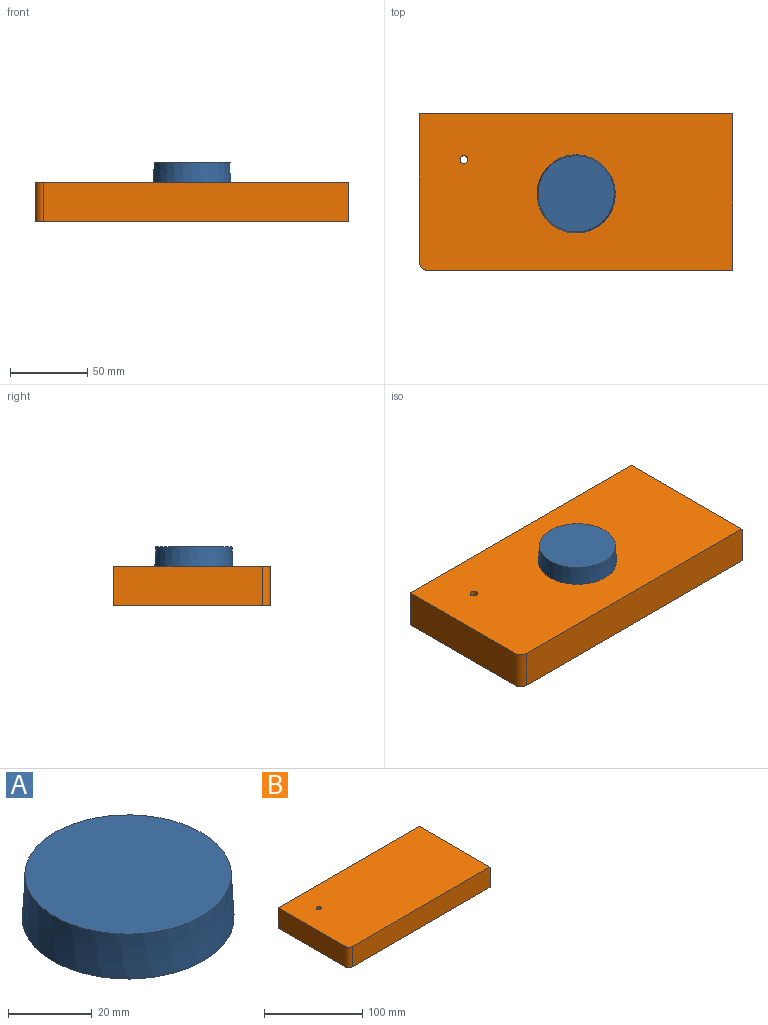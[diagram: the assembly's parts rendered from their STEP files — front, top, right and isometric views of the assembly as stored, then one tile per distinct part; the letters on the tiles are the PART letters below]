
ASSEMBLY  parts=2 mates=1
PART A: 3 faces, bbox 50.8x50.8x12.7 mm
  f0: plane 50.8x50.8mm, normal (0,0,-1), area 2026.8mm2, adj f1
  f1: cone r=25.4mm half-angle=3deg, axis (0,0,-1), area 2003mm2, adj f0,f2
  f2: plane 49.47x49.47mm, normal (0,0,1), area 1922mm2, adj f1
PART B: 8 faces, bbox 203.2x101.6x25.4 mm
  f0: plane 96.52x25.4mm, normal (-1,0,0), area 2451.6mm2, adj f3,f4,f5,f7
  f1: plane 198.12x25.4mm, normal (0,-1,0), area 5032.2mm2, adj f2,f4,f5,f7
  f2: plane 101.6x25.4mm, normal (1,0,0), area 2580.6mm2, adj f1,f3,f4,f5
  f3: plane 203.2x25.4mm, normal (0,1,0), area 5161.3mm2, adj f0,f2,f4,f5
  f4: plane 203.2x101.6mm, normal (0,0,1), area 20619.1mm2, adj f0,f1,f2,f3,f6,f7
  f5: plane 203.2x101.6mm, normal (0,0,-1), area 20619.1mm2, adj f0,f1,f2,f3,f6,f7
  f6: cylinder r=2.55mm len=25.4mm, axis (0,0,1), area 407.4mm2, adj f4,f5
  f7: cylinder r=5.08mm len=25.4mm, axis (0,0,-1), area 202.7mm2, adj f0,f1,f4,f5
PLACE A rot(axis=(0,0,1),90deg) t=(0.1,-1.28,0)mm
PLACE B at identity fixed
MATE planar B.f4 <-> A.f1  axis (0,0,1) through (0.1,-0.01,25.4)mm
